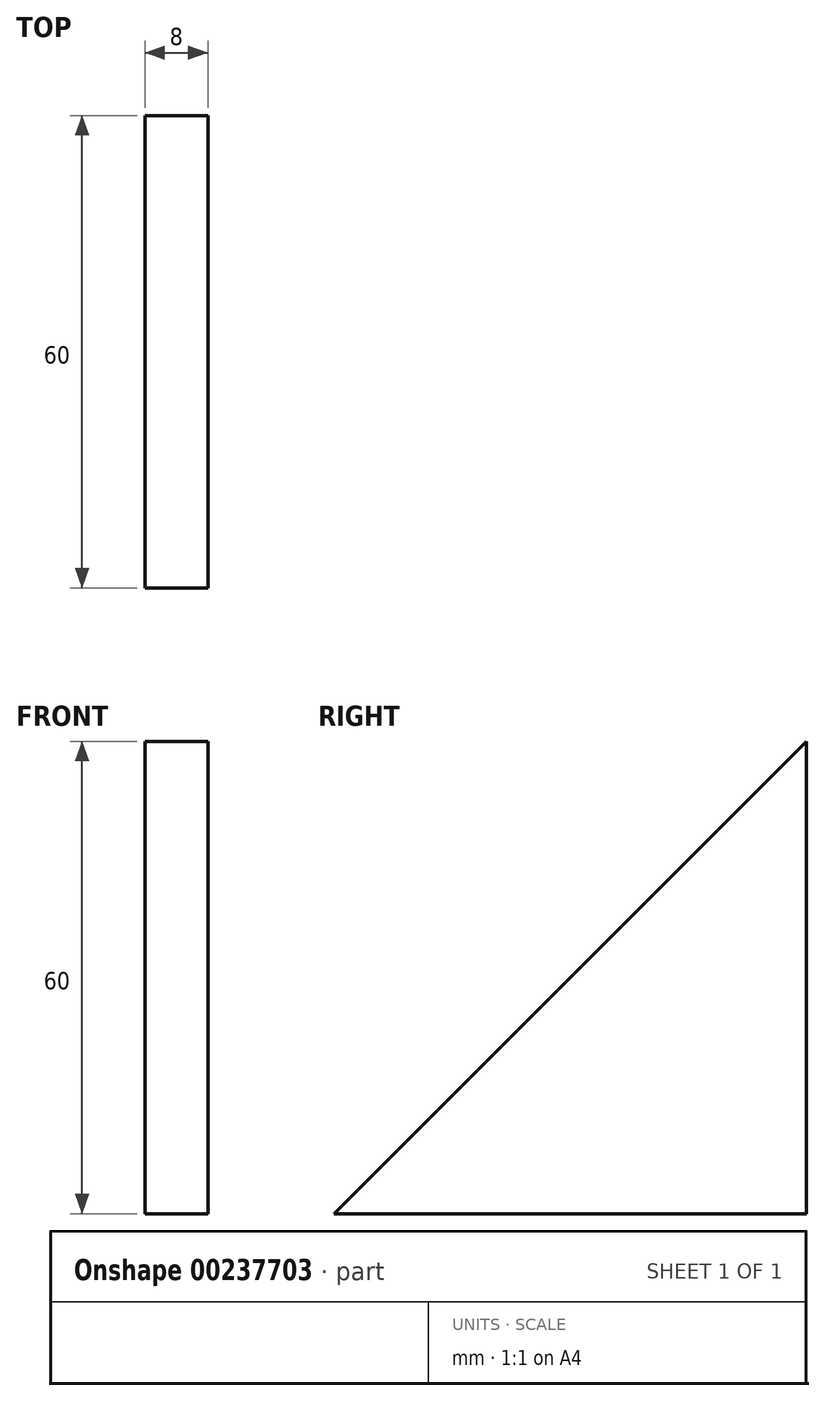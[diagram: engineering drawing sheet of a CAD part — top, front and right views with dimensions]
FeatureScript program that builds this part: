
annotation { "Feature Type Name" : "Feature", "Feature Type Description" : "" }
export const myFeature = defineFeature(function(context is Context, id is Id, definition is map)
    precondition{}
    {
        {
            var Q0;
            Q0=qCreatedBy(makeId("Right.planeOp"),FACE);
            var sketch = newSketch(context, id + "F0", { "sketchPlane" : qUnion([Q0])});
            skLineSegment(sketch, "E0.top", {"start": v(30, -30) * mm, "end": v(-30, -30) * mm});
            skLineSegment(sketch, "E0.left", {"start": v(30, 30) * mm, "end": v(30, -30) * mm});
            skPoint(sketch, "E0.middle", {"position": v(0, 0) * mm});
            skLineSegment(sketch, "E1", {"start": v(30, 30) * mm, "end": v(-30, -30) * mm});
            skPoint(sketch, "E0.right.start.orphan", {"position": v(-30, 30) * mm});
            skSolve(sketch);
        }
        {
            var Q0;
            Q0=makeQuery(id+"F0.imprint","IMPRINT",FACE,{"disambiguationData":[TD([[makeQuery(id+"F0.imprint","IMPRINT",EDGE,{"derivedFrom":sQuery(id+"F0.wireOp",EDGE,"E0.top")}),-1.0]])]});
            extrude(context, id + "F1", {"entities" : qUnion([Q0]), "depth" : 8 * mm});
        }
    });
